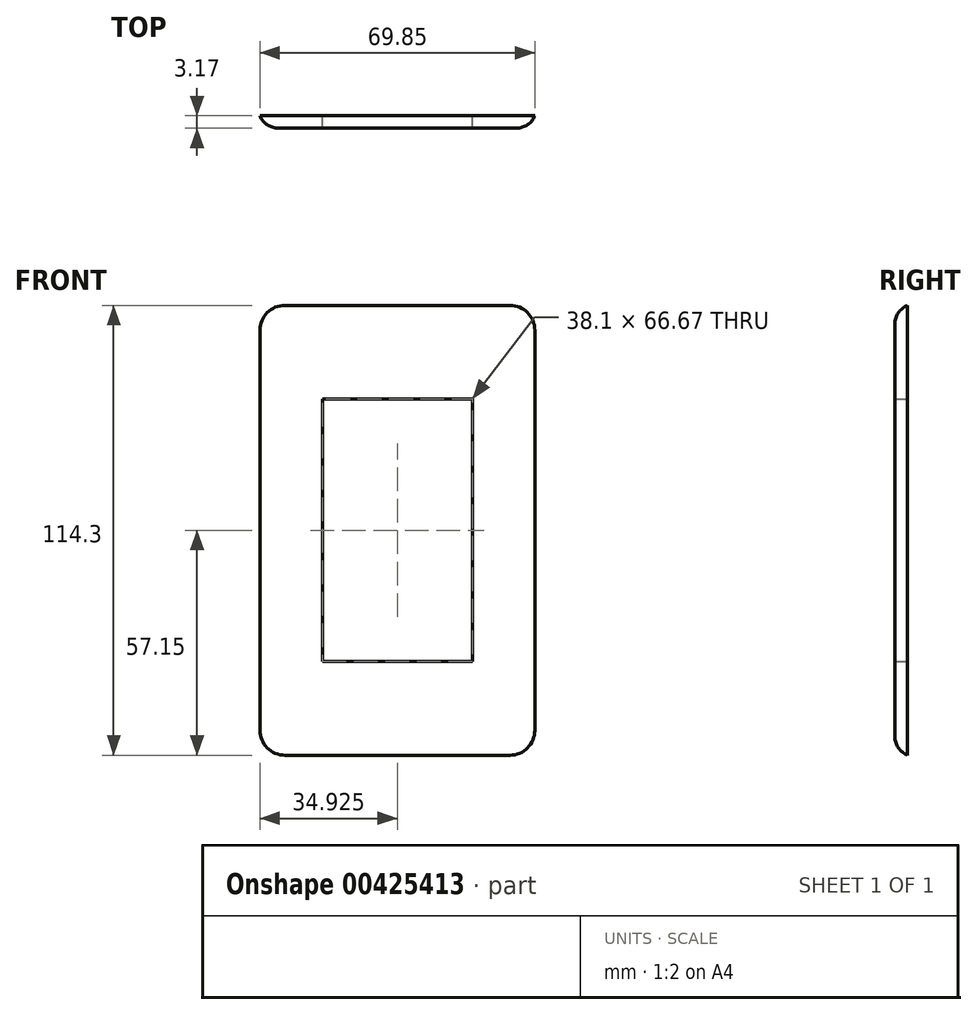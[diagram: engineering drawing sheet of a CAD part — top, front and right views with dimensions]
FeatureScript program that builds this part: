
annotation { "Feature Type Name" : "Feature", "Feature Type Description" : "" }
export const myFeature = defineFeature(function(context is Context, id is Id, definition is map)
    precondition{}
    {
        {
            var Q0;
            Q0=qCreatedBy(makeId("Front.planeOp"),FACE);
            var sketch = newSketch(context, id + "F0", { "sketchPlane" : qUnion([Q0])});
            skLineSegment(sketch, "E0.bottom", {"start": v(6.35, 0) * mm, "end": v(63.5, 0) * mm});
            skLineSegment(sketch, "E0.top", {"start": v(6.35, 114.3) * mm, "end": v(63.5, 114.3) * mm});
            skLineSegment(sketch, "E0.left", {"start": v(0, 6.35) * mm, "end": v(0, 107.95) * mm});
            skLineSegment(sketch, "E0.right", {"start": v(69.85, 6.35) * mm, "end": v(69.85, 107.95) * mm});
            skLineSegment(sketch, "E1.bottom", {"start": v(15.87, 90.49) * mm, "end": v(53.97, 90.49) * mm});
            skLineSegment(sketch, "E1.top", {"start": v(15.88, 23.81) * mm, "end": v(53.98, 23.81) * mm});
            skLineSegment(sketch, "E1.left", {"start": v(15.87, 90.49) * mm, "end": v(15.88, 23.81) * mm});
            skLineSegment(sketch, "E1.right", {"start": v(53.97, 90.49) * mm, "end": v(53.98, 23.81) * mm});
            skPoint(sketch, "E2.visualSharp", {"position": v(0, 114.3) * mm});
            skArc(sketch, "E2.filletArc", {"start": v(6.35, 114.3) * mm, "mid": v(1.86, 112.44) * mm, "end": v(0, 107.95) * mm});
            skPoint(sketch, "E3.visualSharp", {"position": v(69.85, 114.3) * mm});
            skArc(sketch, "E3.filletArc", {"start": v(69.85, 107.95) * mm, "mid": v(68, 112.44) * mm, "end": v(63.5, 114.3) * mm});
            skPoint(sketch, "E4.visualSharp", {"position": v(69.85, 0) * mm});
            skArc(sketch, "E4.filletArc", {"start": v(63.5, 0) * mm, "mid": v(68, 1.86) * mm, "end": v(69.85, 6.35) * mm});
            skPoint(sketch, "E5.visualSharp", {"position": v(0, 0) * mm});
            skArc(sketch, "E5.filletArc", {"start": v(0, 6.35) * mm, "mid": v(1.86, 1.86) * mm, "end": v(6.35, 0) * mm});
            skSolve(sketch);
        }
        {
            var Q0;
            Q0=makeQuery(id+"F0.imprint","IMPRINT",FACE,{"disambiguationData":[TD([[makeQuery(id+"F0.imprint","IMPRINT",EDGE,{"derivedFrom":sQuery(id+"F0.wireOp",EDGE,"E0.bottom")}),1.0]])]});
            extrude(context, id + "F1", {"entities" : qUnion([Q0]), "depth" : 3.17 * mm});
        }
        {
            var Q0;
            Q0=makeQuery(id+"F1.opExtrude","CAP_EDGE",EDGE,{"disambiguationData":[OSD([sQuery(id+"F0.wireOp",EDGE,"E0.top")])],"isStart":false});
            fillet(context, id + "F2", {"entities" : qUnion([Q0]), "radius" : 5.08 * mm, "tangentPropagation" : true, "allowEdgeOverflow" : false});
        }
    });
